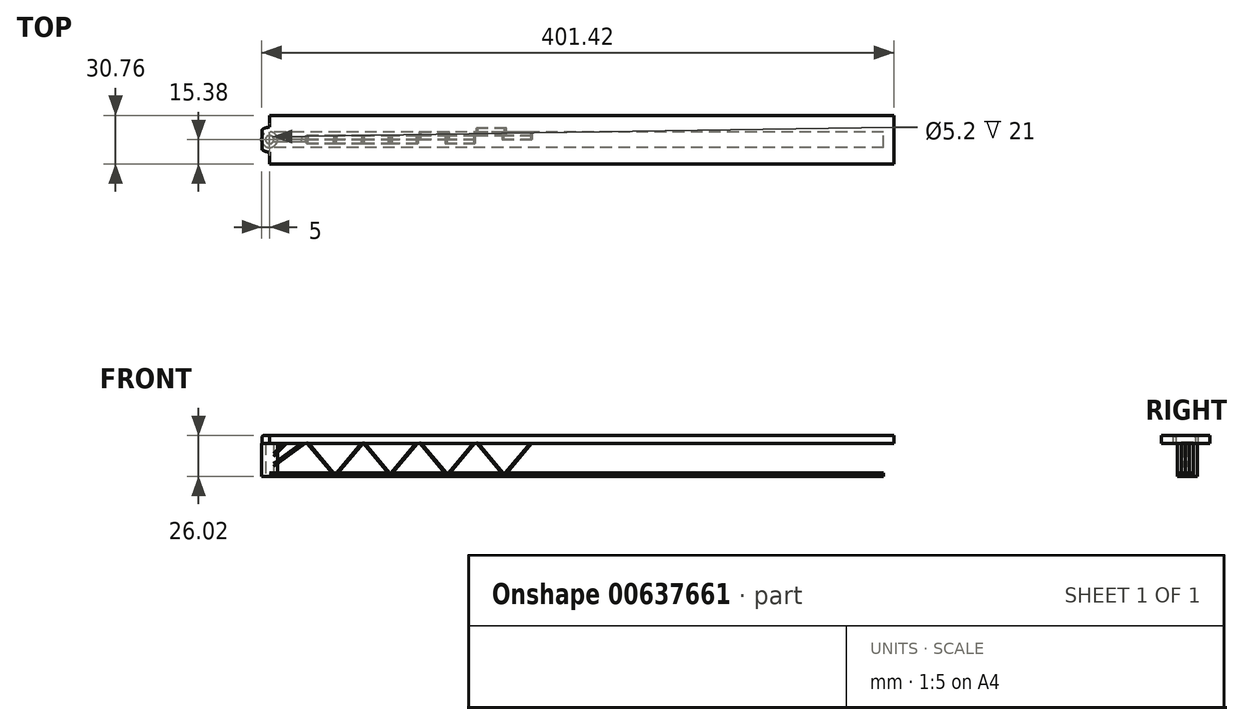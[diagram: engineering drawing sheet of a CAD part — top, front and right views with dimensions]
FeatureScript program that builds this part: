
annotation { "Feature Type Name" : "Feature", "Feature Type Description" : "" }
export const myFeature = defineFeature(function(context is Context, id is Id, definition is map)
    precondition{}
    {
        {
            var Q0;
            Q0=qCreatedBy(makeId("Top.planeOp"),FACE);
            var sketch = newSketch(context, id + "F0", { "sketchPlane" : qUnion([Q0])});
            skCircle(sketch, "E0", {"center": v(0, 0) * mm, "radius": 2.6 * mm});
            skSolve(sketch);
        }
        {
            var Q0;
            Q0=qCreatedBy(makeId("Top.planeOp"),FACE);
            var sketch = newSketch(context, id + "F1", { "sketchPlane" : qUnion([Q0])});
            skCircle(sketch, "E1", {"center": v(0, 0) * mm, "radius": 5 * mm});
            skSolve(sketch);
        }
        {
            var Q0;
            Q0=makeQuery(id+"F1.imprint","IMPRINT",FACE,{"disambiguationData":[TD([[makeQuery(id+"F1.imprint","IMPRINT",EDGE,{"derivedFrom":sQuery(id+"F1.wireOp",EDGE,"E1")}),1.0]])]});
            extrude(context, id + "F2", {"entities" : qUnion([Q0]), "depth" : 21 * mm, "offsetDistance" : 25.4 * mm});
        }
        {
            var Q0;
            Q0=makeQuery(id+"F0.imprint","IMPRINT",FACE,{"disambiguationData":[TD([[makeQuery(id+"F0.imprint","IMPRINT",EDGE,{"derivedFrom":sQuery(id+"F0.wireOp",EDGE,"E0")}),1.0]])]});
            extrude(context, id + "F3", {"entities" : qUnion([Q0]), "operationType" : NewBodyOperationType.REMOVE, "depth" : 22.53 * mm, "offsetDistance" : 25.4 * mm});
        }
        {
            var Q0;
            Q0=qCreatedBy(makeId("Front.planeOp"),FACE);
            var sketch = newSketch(context, id + "F4", { "sketchPlane" : qUnion([Q0])});
            skLineSegment(sketch, "E2", {"start": v(-4.85, 21) * mm, "end": v(-4.85, 24.75) * mm});
            skLineSegment(sketch, "E3", {"start": v(-3.58, 26.02) * mm, "end": v(396.42, 26.02) * mm});
            skLineSegment(sketch, "E4", {"start": v(396.42, 26.02) * mm, "end": v(396.42, 21) * mm});
            skLineSegment(sketch, "E5", {"start": v(396.42, 21) * mm, "end": v(3, 21) * mm});
            skPoint(sketch, "E6.visualSharp", {"position": v(-4.85, 26.02) * mm});
            skArc(sketch, "E6.filletArc", {"start": v(-3.58, 26.02) * mm, "mid": v(-4.48, 25.65) * mm, "end": v(-4.85, 24.75) * mm});
            skLineSegment(sketch, "E7", {"start": v(3, 21) * mm, "end": v(-4.85, 21) * mm});
            skSolve(sketch);
        }
        {
            var Q0;
            Q0=makeQuery(id+"F4.imprint","IMPRINT",FACE,{"disambiguationData":[TD([[makeQuery(id+"F4.imprint","IMPRINT",EDGE,{"derivedFrom":sQuery(id+"F4.wireOp",EDGE,"E2")}),-1.0]])]});
            extrude(context, id + "F5", {"entities" : qUnion([Q0]), "depth" : 22.86 * mm, "offsetDistance" : 25.4 * mm});
        }
        {
            var Q0;
            Q0=makeQuery(id+"F5.opExtrude","CAP_FACE",FACE,{"disambiguationData":[OSD([sQuery(id+"F4.wireOp",EDGE,"E2"),sQuery(id+"F4.wireOp",EDGE,"E3"),sQuery(id+"F4.wireOp",EDGE,"E4"),sQuery(id+"F4.wireOp",EDGE,"E5"),sQuery(id+"F4.wireOp",EDGE,"E6.filletArc"),sQuery(id+"F4.wireOp",EDGE,"E7")])],"isStart":true});
            extrude(context, id + "F6", {"entities" : qUnion([Q0]), "operationType" : NewBodyOperationType.ADD, "depth" : 22.86 * mm, "offsetDistance" : 25.4 * mm});
        }
        {
            var Q0;
            {var subQ0=sQuery(id+"F4.wireOp",EDGE,"E3");Q0=makeQuery(id+"F6.boolean.opBoolean","MERGE",FACE,{"derivedFrom":[makeQuery(id+"F5.opExtrude","SWEPT_FACE",FACE,{"disambiguationData":[OSD([subQ0])]}),makeQuery(id+"F6.opExtrude","SWEPT_FACE",FACE,{"disambiguationData":[OSD([subQ0])]})]});}
            var sketch = newSketch(context, id + "F7", { "sketchPlane" : qUnion([Q0])});
            skLineSegment(sketch, "E8.bottom", {"start": v(73.66, -10.5) * mm, "end": v(94.66, -10.5) * mm});
            skLineSegment(sketch, "E8.top", {"start": v(73.66, 10.5) * mm, "end": v(94.66, 10.5) * mm});
            skLineSegment(sketch, "E8.left", {"start": v(73.66, -10.5) * mm, "end": v(73.66, 10.5) * mm});
            skLineSegment(sketch, "E8.right", {"start": v(94.66, -10.5) * mm, "end": v(94.66, 10.5) * mm});
            skPoint(sketch, "E8.middle", {"position": v(84.16, 0) * mm});
            skSolve(sketch);
        }
        {
            var Q0;
            {var subQ0=sQuery(id+"F4.wireOp",EDGE,"E7");var subQ1=sQuery(id+"F4.wireOp",EDGE,"E5");Q0=makeQuery(id+"F6.boolean.opBoolean","MERGE",FACE,{"derivedFrom":[makeQuery(id+"F5.opExtrude","SWEPT_FACE",FACE,{"disambiguationData":[OSD([subQ1,subQ0])]}),makeQuery(id+"F6.opExtrude","SWEPT_FACE",FACE,{"disambiguationData":[OSD([subQ1,subQ0])]})]});}
            var sketch = newSketch(context, id + "F8", { "sketchPlane" : qUnion([Q0])});
            skLineSegment(sketch, "E9", {"start": v(-4.85, -22.86) * mm, "end": v(-4.85, 22.86) * mm});
            skArc(sketch, "E10", {"start": v(0, 7.9) * mm, "mid": v(-7.9, 0) * mm, "end": v(0, -7.9) * mm});
            skLineSegment(sketch, "E11", {"start": v(0, -22.86) * mm, "end": v(0, -7.9) * mm});
            skLineSegment(sketch, "E12", {"start": v(-4.85, 22.86) * mm, "end": v(0, 22.86) * mm});
            skLineSegment(sketch, "E13", {"start": v(0, 22.86) * mm, "end": v(0, 7.9) * mm});
            skLineSegment(sketch, "E14", {"start": v(-4.85, -22.86) * mm, "end": v(0, -22.86) * mm});
            skLineSegment(sketch, "E15", {"start": v(10.56, -22.86) * mm, "end": v(10.56, 22.86) * mm});
            skSolve(sketch);
        }
        {
            var Q0;
            Q0=qSketchRegion(id+"F8",true);
            extrude(context, id + "F9", {"entities" : qUnion([Q0]), "operationType" : NewBodyOperationType.REMOVE, "oppositeDirection" : true, "depth" : 25.4 * mm, "offsetDistance" : 25.4 * mm});
        }
        {
            var Q0;
            Q0=makeQuery(id+"FSWrnr269RCgbZk_2.boolean.opBoolean","SPLIT",EDGE,{"derivedFrom":makeQuery(id+"F2.opExtrude","CAP_EDGE",EDGE,{"disambiguationData":[OSD([sQuery(id+"F1.wireOp",EDGE,"E1")])],"isStart":false})});
            fillet(context, id + "F10", {"entities" : qUnion([Q0]), "radius" : 0.3 * mm, "tangentPropagation" : true, "allowEdgeOverflow" : false});
        }
        {
            var Q0;
            Q0=qCreatedBy(makeId("Front.planeOp"),FACE);
            var sketch = newSketch(context, id + "F11", { "sketchPlane" : qUnion([Q0])});
            skLineSegment(sketch, "E16", {"start": v(10.69, 21.02) * mm, "end": v(2.5, 12.74) * mm});
            skLineSegment(sketch, "E17", {"start": v(10.69, 21.02) * mm, "end": v(8.95, 21.02) * mm});
            skLineSegment(sketch, "E18", {"start": v(8.95, 21.02) * mm, "end": v(2.59, 14.59) * mm});
            skLineSegment(sketch, "E19", {"start": v(2.59, 14.59) * mm, "end": v(2.5, 12.74) * mm});
            skSolve(sketch);
        }
        {
            var Q0;
            Q0=makeQuery(id+"F11.imprint","IMPRINT",FACE,{"disambiguationData":[TD([[makeQuery(id+"F11.imprint","IMPRINT",EDGE,{"derivedFrom":sQuery(id+"F11.wireOp",EDGE,"E16")}),-1.0]])]});
            extrude(context, id + "F12", {"entities" : qUnion([Q0]), "depth" : 1.52 * mm, "offsetDistance" : 25.4 * mm});
        }
        {
            var Q0;
            Q0=makeQuery(id+"F12.opExtrude","CAP_FACE",FACE,{"disambiguationData":[OSD([sQuery(id+"F11.wireOp",EDGE,"E16"),sQuery(id+"F11.wireOp",EDGE,"E17"),sQuery(id+"F11.wireOp",EDGE,"E18"),sQuery(id+"F11.wireOp",EDGE,"E19")])],"isStart":true});
            extrude(context, id + "F13", {"entities" : qUnion([Q0]), "depth" : 1.52 * mm, "offsetDistance" : 25.4 * mm});
        }
        {
            var Q0;
            Q0=qSketchRegion(id+"F7",true);
            extrude(context, id + "F14", {"entities" : qUnion([Q0]), "operationType" : NewBodyOperationType.REMOVE, "depth" : 12.95 * mm, "offsetDistance" : 25.4 * mm});
        }
        {
            var Q0;
            Q0=qCreatedBy(makeId("Front.planeOp"),FACE);
            var sketch = newSketch(context, id + "F15", { "sketchPlane" : qUnion([Q0])});
            skLineSegment(sketch, "E20", {"start": v(22.9, 21.28) * mm, "end": v(2.41, 6.35) * mm});
            skLineSegment(sketch, "E21", {"start": v(22.9, 21.28) * mm, "end": v(20.45, 21.28) * mm});
            skLineSegment(sketch, "E22", {"start": v(20.45, 21.28) * mm, "end": v(2.5, 8.2) * mm});
            skLineSegment(sketch, "E23", {"start": v(2.5, 8.2) * mm, "end": v(2.41, 6.35) * mm});
            skSolve(sketch);
        }
        {
            var Q0;
            Q0=makeQuery(id+"F15.imprint","IMPRINT",FACE,{"disambiguationData":[TD([[makeQuery(id+"F15.imprint","IMPRINT",EDGE,{"derivedFrom":sQuery(id+"F15.wireOp",EDGE,"E20")}),-1.0]])]});
            extrude(context, id + "F16", {"entities" : qUnion([Q0]), "depth" : 1.52 * mm, "offsetDistance" : 25.4 * mm});
        }
        {
            var Q0;
            Q0=qSketchRegion(id+"F15",true);
            extrude(context, id + "F17", {"entities" : qUnion([Q0]), "oppositeDirection" : true, "depth" : 1.52 * mm, "offsetDistance" : 25.4 * mm});
        }
        {
            var Q0;
            {var subQ0=sQuery(id+"F4.wireOp",EDGE,"E3");Q0=makeQuery(id+"F6.boolean.opBoolean","MERGE",FACE,{"derivedFrom":[makeQuery(id+"F5.opExtrude","SWEPT_FACE",FACE,{"disambiguationData":[OSD([subQ0])]}),makeQuery(id+"F6.opExtrude","SWEPT_FACE",FACE,{"disambiguationData":[OSD([subQ0])]})]});}
            var sketch = newSketch(context, id + "F18", { "sketchPlane" : qUnion([Q0])});
            skLineSegment(sketch, "E24", {"start": v(0, 15.38) * mm, "end": v(396.42, 15.38) * mm});
            skLineSegment(sketch, "E25", {"start": v(396.42, 15.38) * mm, "end": v(396.42, 22.86) * mm});
            skLineSegment(sketch, "E26", {"start": v(396.42, 22.86) * mm, "end": v(0, 22.86) * mm});
            skLineSegment(sketch, "E27", {"start": v(0, 22.86) * mm, "end": v(0, 15.38) * mm});
            skLineSegment(sketch, "E28", {"start": v(0, -15.38) * mm, "end": v(396.42, -15.38) * mm});
            skLineSegment(sketch, "E29", {"start": v(0, -15.38) * mm, "end": v(0, -22.86) * mm});
            skLineSegment(sketch, "E30", {"start": v(0, -22.86) * mm, "end": v(396.42, -22.86) * mm});
            skLineSegment(sketch, "E31", {"start": v(396.42, -22.86) * mm, "end": v(396.42, -15.38) * mm});
            skSolve(sketch);
        }
        {
            var Q0;
            Q0 = qSketchRegion(id + "F18", true);
            extrude(context, id + "F19", {"entities" : qUnion([Q0]), "operationType" : NewBodyOperationType.REMOVE, "oppositeDirection" : true, "depth" : 25.4 * mm, "offsetDistance" : 25.4 * mm});
        }
        {
            var Q0;
            Q0=qCreatedBy(makeId("Right.planeOp"),FACE);
            var sketch = newSketch(context, id + "F20", { "sketchPlane" : qUnion([Q0])});
            skLineSegment(sketch, "E32.bottom", {"start": v(-5, 2.35) * mm, "end": v(4.99, 2.35) * mm});
            skLineSegment(sketch, "E32.top", {"start": v(-5, 0) * mm, "end": v(4.99, 0) * mm});
            skLineSegment(sketch, "E32.left", {"start": v(-5, 2.35) * mm, "end": v(-5, 0) * mm});
            skLineSegment(sketch, "E32.right", {"start": v(4.99, 2.35) * mm, "end": v(4.99, 0) * mm});
            skSolve(sketch);
        }
        {
            var Q0;
            Q0 = qSketchRegion(id + "F20", true);
            extrude(context, id + "F21", {"entities" : qUnion([Q0]), "depth" : 390 * mm, "offsetDistance" : 25.4 * mm});
        }
        {
            var Q0;
            Q0=makeQuery(id+"F21.opExtrude","SWEPT_FACE",FACE,{"disambiguationData":[OSD([sQuery(id+"F20.wireOp",EDGE,"E32.top")])]});
            var sketch = newSketch(context, id + "F22", { "sketchPlane" : qUnion([Q0])});
            skArc(sketch, "E33", {"start": v(0, -2.62) * mm, "mid": v(2.6, 0) * mm, "end": v(0, 2.6) * mm});
            skLineSegment(sketch, "E34", {"start": v(0, 2.6) * mm, "end": v(0, -2.62) * mm});
            skSolve(sketch);
        }
        {
            var Q0;
            Q0 = qSketchRegion(id + "F22", true);
            extrude(context, id + "F23", {"entities" : qUnion([Q0]), "operationType" : NewBodyOperationType.REMOVE, "oppositeDirection" : true, "depth" : 2.03 * mm, "offsetDistance" : 25 * mm});
        }
        {
            var Q0;
            Q0=qCreatedBy(makeId("Front.planeOp"),FACE);
            var sketch = newSketch(context, id + "F24", { "sketchPlane" : qUnion([Q0])});
            skLineSegment(sketch, "E35", {"start": v(23.5, 21.45) * mm, "end": v(41.5, 0) * mm});
            skLineSegment(sketch, "E36", {"start": v(41.5, 0) * mm, "end": v(42.58, 0) * mm});
            skLineSegment(sketch, "E37", {"start": v(42.58, 0) * mm, "end": v(24.57, 21.45) * mm});
            skLineSegment(sketch, "E38", {"start": v(24.57, 21.45) * mm, "end": v(23.5, 21.45) * mm});
            skSolve(sketch);
        }
        {
            var Q0;
            Q0=makeQuery(id+"F24.imprint","IMPRINT",FACE,{"disambiguationData":[TD([[makeQuery(id+"F24.imprint","IMPRINT",EDGE,{"derivedFrom":sQuery(id+"F24.wireOp",EDGE,"E35")}),1.0]])]});
            extrude(context, id + "F25", {"entities" : qUnion([Q0]), "depth" : 2.5 * mm, "offsetDistance" : 25 * mm});
        }
        {
            var Q0;
            Q0 = qSketchRegion(id + "F24", true);
            extrude(context, id + "F26", {"entities" : qUnion([Q0]), "oppositeDirection" : true, "depth" : 2.5 * mm, "offsetDistance" : 25 * mm});
        }
        {
            var Q0;
            Q0=qCreatedBy(makeId("Front.planeOp"),FACE);
            var sketch = newSketch(context, id + "F27", { "sketchPlane" : qUnion([Q0])});
            skLineSegment(sketch, "E39.MirrorCS", {"start": v(41.65, 0) * mm, "end": v(40.57, 0) * mm});
            skLineSegment(sketch, "E40.MirrorCS", {"start": v(58.58, 21.45) * mm, "end": v(59.65, 21.45) * mm});
            skLineSegment(sketch, "E41.MirrorCS", {"start": v(59.65, 21.45) * mm, "end": v(41.65, 0) * mm});
            skLineSegment(sketch, "E42.MirrorCS", {"start": v(40.57, 0) * mm, "end": v(58.58, 21.45) * mm});
            skSolve(sketch);
        }
        {
            var Q0;
            Q0=makeQuery(id+"F27.imprint","IMPRINT",FACE,{"disambiguationData":[TD([[makeQuery(id+"F27.imprint","IMPRINT",EDGE,{"derivedFrom":sQuery(id+"F27.wireOp",EDGE,"E39.MirrorCS")}),-1.0]])]});
            extrude(context, id + "F28", {"entities" : qUnion([Q0]), "depth" : 2.5 * mm, "offsetDistance" : 25 * mm});
        }
        {
            var Q0;
            Q0 = qSketchRegion(id + "F27", true);
            extrude(context, id + "F29", {"entities" : qUnion([Q0]), "oppositeDirection" : true, "depth" : 2.5 * mm, "offsetDistance" : 25 * mm});
        }
        {
            var Q0;
            Q0=makeQuery(id+"F25.opExtrude","SWEPT_BODY",BODY,{"disambiguationData":[OSD([sQuery(id+"F24.wireOp",EDGE,"E35"),sQuery(id+"F24.wireOp",EDGE,"E36"),sQuery(id+"F24.wireOp",EDGE,"E37"),sQuery(id+"F24.wireOp",EDGE,"E38")])]});
            transform(context, id + "F30", {"entities" : qUnion([Q0]), "transformType" : TransformType.TRANSLATION_3D, "dx" : 35.7 * mm, "dy" : 0 * mm, "dz" : 0 * mm, "makeCopy" : true});
        }
        {
            var Q0;
            Q0=makeQuery(id+"F30.opPattern","COPY",BODY,{"derivedFrom":makeQuery(id+"F25.opExtrude","SWEPT_BODY",BODY,{"disambiguationData":[OSD([sQuery(id+"F24.wireOp",EDGE,"E35"),sQuery(id+"F24.wireOp",EDGE,"E36"),sQuery(id+"F24.wireOp",EDGE,"E37"),sQuery(id+"F24.wireOp",EDGE,"E38")])]}),"instanceName":"1"});
            transform(context, id + "F31", {"entities" : qUnion([Q0]), "transformType" : TransformType.TRANSLATION_3D, "dx" : 0 * mm, "dy" : 2.5 * mm, "dz" : 0 * mm, "makeCopy" : true});
        }
        {
            var Q0;
            Q0=makeQuery(id+"F29.opExtrude","SWEPT_BODY",BODY,{"disambiguationData":[OSD([sQuery(id+"F27.wireOp",EDGE,"E39.MirrorCS"),sQuery(id+"F27.wireOp",EDGE,"E40.MirrorCS"),sQuery(id+"F27.wireOp",EDGE,"E41.MirrorCS"),sQuery(id+"F27.wireOp",EDGE,"E42.MirrorCS")])]});
            transform(context, id + "F32", {"entities" : qUnion([Q0]), "transformType" : TransformType.TRANSLATION_3D, "dx" : 34.6 * mm, "dy" : 0 * mm, "dz" : 0 * mm, "makeCopy" : true});
        }
        {
            var Q0;
            Q0=makeQuery(id+"F32.opPattern","COPY",BODY,{"derivedFrom":makeQuery(id+"F29.opExtrude","SWEPT_BODY",BODY,{"disambiguationData":[OSD([sQuery(id+"F27.wireOp",EDGE,"E39.MirrorCS"),sQuery(id+"F27.wireOp",EDGE,"E40.MirrorCS"),sQuery(id+"F27.wireOp",EDGE,"E41.MirrorCS"),sQuery(id+"F27.wireOp",EDGE,"E42.MirrorCS")])]}),"instanceName":"1"});
            transform(context, id + "F33", {"entities" : qUnion([Q0]), "transformType" : TransformType.TRANSLATION_3D, "dx" : 0 * mm, "dy" : -2.5 * mm, "dz" : 0 * mm, "makeCopy" : true});
        }
        {
            var Q0;
            Q0=makeQuery(id+"F31.opPattern","COPY",BODY,{"derivedFrom":makeQuery(id+"F30.opPattern","COPY",BODY,{"derivedFrom":makeQuery(id+"F25.opExtrude","SWEPT_BODY",BODY,{"disambiguationData":[OSD([sQuery(id+"F24.wireOp",EDGE,"E35"),sQuery(id+"F24.wireOp",EDGE,"E36"),sQuery(id+"F24.wireOp",EDGE,"E37"),sQuery(id+"F24.wireOp",EDGE,"E38")])]}),"instanceName":"1"}),"instanceName":"1"});
            transform(context, id + "F34", {"entities" : qUnion([Q0]), "transformType" : TransformType.TRANSLATION_3D, "dx" : 36 * mm, "dy" : 0 * mm, "dz" : 0 * mm, "makeCopy" : true});
        }
        {
            var Q0;
            Q0=makeQuery(id+"F34.opPattern","COPY",BODY,{"derivedFrom":makeQuery(id+"F31.opPattern","COPY",BODY,{"derivedFrom":makeQuery(id+"F30.opPattern","COPY",BODY,{"derivedFrom":makeQuery(id+"F25.opExtrude","SWEPT_BODY",BODY,{"disambiguationData":[OSD([sQuery(id+"F24.wireOp",EDGE,"E35"),sQuery(id+"F24.wireOp",EDGE,"E36"),sQuery(id+"F24.wireOp",EDGE,"E37"),sQuery(id+"F24.wireOp",EDGE,"E38")])]}),"instanceName":"1"}),"instanceName":"1"}),"instanceName":"1"});
            transform(context, id + "F35", {"entities" : qUnion([Q0]), "transformType" : TransformType.TRANSLATION_3D, "dx" : 0 * mm, "dy" : 2.5 * mm, "dz" : 0 * mm, "makeCopy" : true});
        }
        {
            var Q0;
            Q0=makeQuery(id+"F33.opPattern","COPY",BODY,{"derivedFrom":makeQuery(id+"F32.opPattern","COPY",BODY,{"derivedFrom":makeQuery(id+"F29.opExtrude","SWEPT_BODY",BODY,{"disambiguationData":[OSD([sQuery(id+"F27.wireOp",EDGE,"E39.MirrorCS"),sQuery(id+"F27.wireOp",EDGE,"E40.MirrorCS"),sQuery(id+"F27.wireOp",EDGE,"E41.MirrorCS"),sQuery(id+"F27.wireOp",EDGE,"E42.MirrorCS")])]}),"instanceName":"1"}),"instanceName":"1"});
            transform(context, id + "F36", {"entities" : qUnion([Q0]), "transformType" : TransformType.TRANSLATION_3D, "dx" : 36.4 * mm, "dy" : 0 * mm, "dz" : 0 * mm, "makeCopy" : true});
        }
        {
            var Q0;
            Q0=makeQuery(id+"F36.opPattern","COPY",BODY,{"derivedFrom":makeQuery(id+"F33.opPattern","COPY",BODY,{"derivedFrom":makeQuery(id+"F32.opPattern","COPY",BODY,{"derivedFrom":makeQuery(id+"F29.opExtrude","SWEPT_BODY",BODY,{"disambiguationData":[OSD([sQuery(id+"F27.wireOp",EDGE,"E39.MirrorCS"),sQuery(id+"F27.wireOp",EDGE,"E40.MirrorCS"),sQuery(id+"F27.wireOp",EDGE,"E41.MirrorCS"),sQuery(id+"F27.wireOp",EDGE,"E42.MirrorCS")])]}),"instanceName":"1"}),"instanceName":"1"}),"instanceName":"1"});
            transform(context, id + "F37", {"entities" : qUnion([Q0]), "transformType" : TransformType.TRANSLATION_3D, "dx" : 0 * mm, "dy" : 2.5 * mm, "dz" : 0 * mm, "makeCopy" : true});
        }
        {
            var Q0;
            Q0=makeQuery(id+"F35.opPattern","COPY",BODY,{"derivedFrom":makeQuery(id+"F34.opPattern","COPY",BODY,{"derivedFrom":makeQuery(id+"F31.opPattern","COPY",BODY,{"derivedFrom":makeQuery(id+"F30.opPattern","COPY",BODY,{"derivedFrom":makeQuery(id+"F25.opExtrude","SWEPT_BODY",BODY,{"disambiguationData":[OSD([sQuery(id+"F24.wireOp",EDGE,"E35"),sQuery(id+"F24.wireOp",EDGE,"E36"),sQuery(id+"F24.wireOp",EDGE,"E37"),sQuery(id+"F24.wireOp",EDGE,"E38")])]}),"instanceName":"1"}),"instanceName":"1"}),"instanceName":"1"}),"instanceName":"1"});
            transform(context, id + "F38", {"entities" : qUnion([Q0]), "transformType" : TransformType.TRANSLATION_3D, "dx" : 36.1 * mm, "dy" : 0 * mm, "dz" : 0 * mm, "makeCopy" : true});
        }
        {
            var Q0;
            Q0=makeQuery(id+"F38.opPattern","COPY",BODY,{"derivedFrom":makeQuery(id+"F35.opPattern","COPY",BODY,{"derivedFrom":makeQuery(id+"F34.opPattern","COPY",BODY,{"derivedFrom":makeQuery(id+"F31.opPattern","COPY",BODY,{"derivedFrom":makeQuery(id+"F30.opPattern","COPY",BODY,{"derivedFrom":makeQuery(id+"F25.opExtrude","SWEPT_BODY",BODY,{"disambiguationData":[OSD([sQuery(id+"F24.wireOp",EDGE,"E35"),sQuery(id+"F24.wireOp",EDGE,"E36"),sQuery(id+"F24.wireOp",EDGE,"E37"),sQuery(id+"F24.wireOp",EDGE,"E38")])]}),"instanceName":"1"}),"instanceName":"1"}),"instanceName":"1"}),"instanceName":"1"}),"instanceName":"1"});
            transform(context, id + "F39", {"entities" : qUnion([Q0]), "transformType" : TransformType.TRANSLATION_3D, "dx" : 0 * mm, "dy" : 2.5 * mm, "dz" : 0 * mm, "makeCopy" : true});
        }
        {
            var Q0;
            Q0=makeQuery(id+"F37.opPattern","COPY",BODY,{"derivedFrom":makeQuery(id+"F36.opPattern","COPY",BODY,{"derivedFrom":makeQuery(id+"F33.opPattern","COPY",BODY,{"derivedFrom":makeQuery(id+"F32.opPattern","COPY",BODY,{"derivedFrom":makeQuery(id+"F29.opExtrude","SWEPT_BODY",BODY,{"disambiguationData":[OSD([sQuery(id+"F27.wireOp",EDGE,"E39.MirrorCS"),sQuery(id+"F27.wireOp",EDGE,"E40.MirrorCS"),sQuery(id+"F27.wireOp",EDGE,"E41.MirrorCS"),sQuery(id+"F27.wireOp",EDGE,"E42.MirrorCS")])]}),"instanceName":"1"}),"instanceName":"1"}),"instanceName":"1"}),"instanceName":"1"});
            transform(context, id + "F40", {"entities" : qUnion([Q0]), "transformType" : TransformType.TRANSLATION_3D, "dx" : 36.1 * mm, "dy" : 0 * mm, "dz" : 0 * mm, "makeCopy" : true});
        }
        {
            var Q0;
            Q0=makeQuery(id+"F40.opPattern","COPY",BODY,{"derivedFrom":makeQuery(id+"F37.opPattern","COPY",BODY,{"derivedFrom":makeQuery(id+"F36.opPattern","COPY",BODY,{"derivedFrom":makeQuery(id+"F33.opPattern","COPY",BODY,{"derivedFrom":makeQuery(id+"F32.opPattern","COPY",BODY,{"derivedFrom":makeQuery(id+"F29.opExtrude","SWEPT_BODY",BODY,{"disambiguationData":[OSD([sQuery(id+"F27.wireOp",EDGE,"E39.MirrorCS"),sQuery(id+"F27.wireOp",EDGE,"E40.MirrorCS"),sQuery(id+"F27.wireOp",EDGE,"E41.MirrorCS"),sQuery(id+"F27.wireOp",EDGE,"E42.MirrorCS")])]}),"instanceName":"1"}),"instanceName":"1"}),"instanceName":"1"}),"instanceName":"1"}),"instanceName":"1"});
            transform(context, id + "F41", {"entities" : qUnion([Q0]), "transformType" : TransformType.TRANSLATION_3D, "dx" : 0 * mm, "dy" : 2.5 * mm, "dz" : 0 * mm, "makeCopy" : true});
        }
    });
